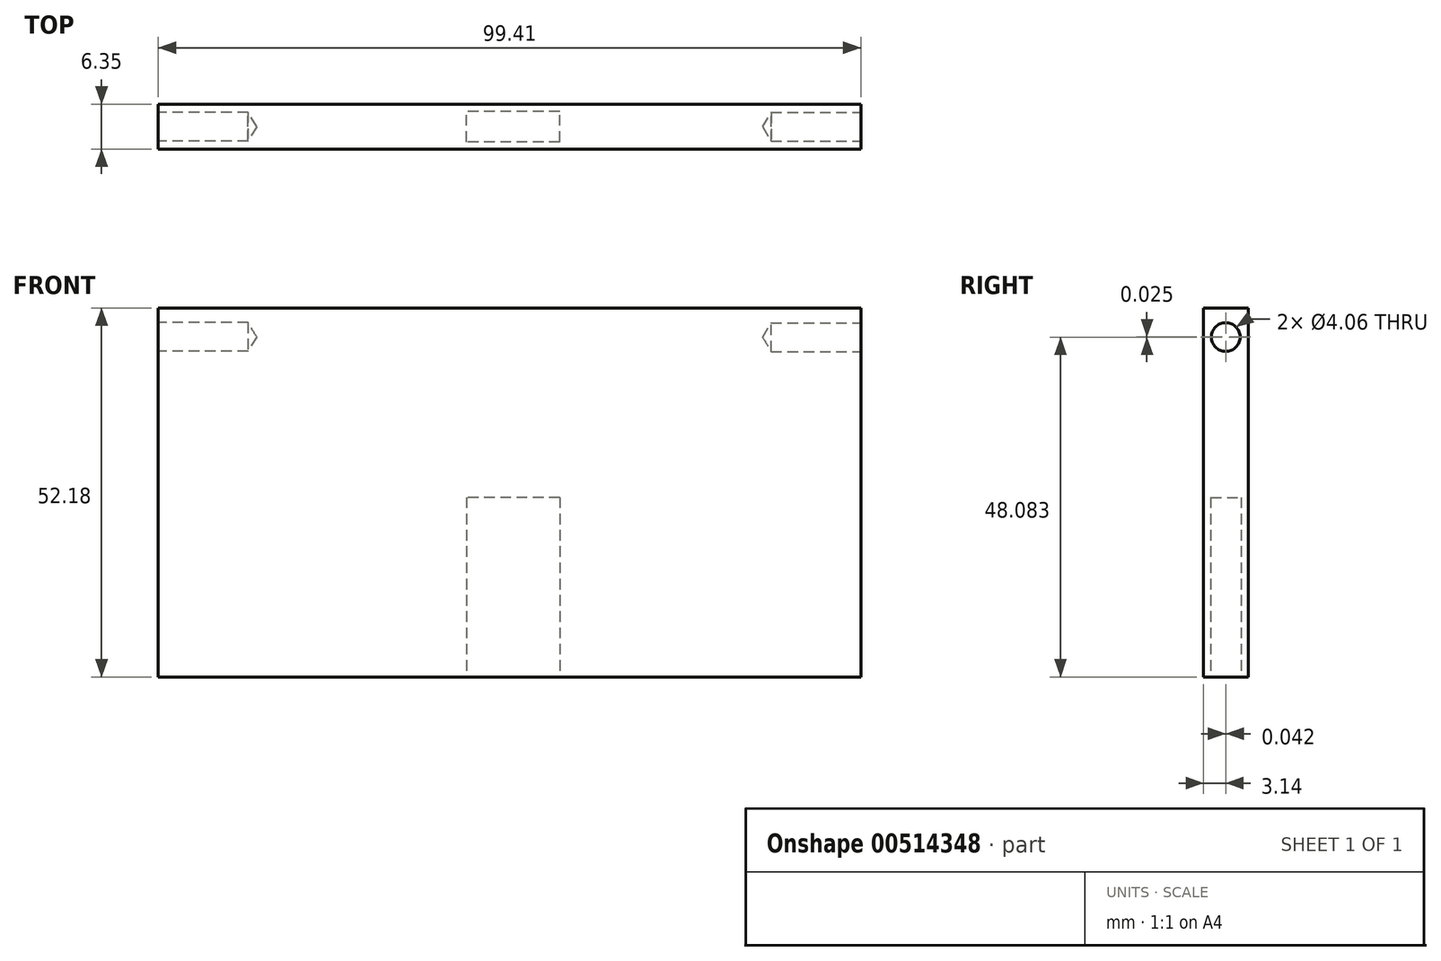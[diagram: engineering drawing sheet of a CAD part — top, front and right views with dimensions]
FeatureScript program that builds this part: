
annotation { "Feature Type Name" : "Feature", "Feature Type Description" : "" }
export const myFeature = defineFeature(function(context is Context, id is Id, definition is map)
    precondition{}
    {
        {
            var Q0;
            Q0=qCreatedBy(makeId("Front.planeOp"),FACE);
            var sketch = newSketch(context, id + "F0", { "sketchPlane" : qUnion([Q0])});
            skLineSegment(sketch, "E0.bottom", {"start": v(-50.2, 52.55) * mm, "end": v(49.21, 52.55) * mm});
            skLineSegment(sketch, "E0.top", {"start": v(-50.2, 0.37) * mm, "end": v(49.21, 0.37) * mm});
            skLineSegment(sketch, "E0.left", {"start": v(-50.2, 52.55) * mm, "end": v(-50.2, 0.37) * mm});
            skLineSegment(sketch, "E0.right", {"start": v(49.21, 52.55) * mm, "end": v(49.21, 0.37) * mm});
            skSolve(sketch);
        }
        {
            var Q0;
            Q0=makeQuery(id+"F0.imprint","IMPRINT",FACE,{"disambiguationData":[TD([[makeQuery(id+"F0.imprint","IMPRINT",EDGE,{"derivedFrom":sQuery(id+"F0.wireOp",EDGE,"E0.bottom")}),-1.0]])]});
            extrude(context, id + "F1", {"entities" : qUnion([Q0]), "depth" : 6.35 * mm});
        }
        {
            var Q0;
            Q0=makeQuery(id+"F1.opExtrude","SWEPT_FACE",FACE,{"disambiguationData":[OSD([sQuery(id+"F0.wireOp",EDGE,"E0.left")])]});
            var sketch = newSketch(context, id + "F2", { "sketchPlane" : qUnion([Q0])});
            skCircle(sketch, "E1", {"center": v(3.17, 48.48) * mm, "radius": 1.98 * mm});
            skSolve(sketch);
        }
        {
            var Q0;
            Q0=makeQuery(id+"F1.opExtrude","SWEPT_FACE",FACE,{"disambiguationData":[OSD([sQuery(id+"F0.wireOp",EDGE,"E0.right")])]});
            var sketch = newSketch(context, id + "F3", { "sketchPlane" : qUnion([Q0])});
            skCircle(sketch, "E2", {"center": v(-3.21, 48.45) * mm, "radius": 1.98 * mm});
            skSolve(sketch);
        }
        {
            var Q0;
            Q0=sQuery(id+"F3.wireOp",VERTEX,"E2.center");
            var Q1;
            Q1=makeQuery(id+"F1.opExtrude","SWEPT_BODY",BODY,{"disambiguationData":[OSD([sQuery(id+"F0.wireOp",EDGE,"E0.bottom"),sQuery(id+"F0.wireOp",EDGE,"E0.top"),sQuery(id+"F0.wireOp",EDGE,"E0.left"),sQuery(id+"F0.wireOp",EDGE,"E0.right")])]});
            hole(context, id + "F4", {"style" : HoleStyle.SIMPLE, "endStyle" : HoleEndStyle.BLIND, "holeDiameter" : 4.06 * mm, "holeDepth" : 12.7 * mm, "isTappedThrough" : true, "tappedDepth" : 12.7 * mm, "tapClearance" : 3, "locations" : qUnion([Q0]), "scope" : qUnion([Q1])});
        }
        {
            var Q0;
            Q0=sQuery(id+"F2.wireOp",VERTEX,"E1.center");
            var Q1;
            Q1=makeQuery(id+"F1.opExtrude","SWEPT_BODY",BODY,{"disambiguationData":[OSD([sQuery(id+"F0.wireOp",EDGE,"E0.bottom"),sQuery(id+"F0.wireOp",EDGE,"E0.top"),sQuery(id+"F0.wireOp",EDGE,"E0.left"),sQuery(id+"F0.wireOp",EDGE,"E0.right")])]});
            hole(context, id + "F5", {"style" : HoleStyle.SIMPLE, "endStyle" : HoleEndStyle.BLIND, "holeDiameter" : 4.06 * mm, "holeDepth" : 12.7 * mm, "isTappedThrough" : true, "tappedDepth" : 12.7 * mm, "tapClearance" : 3, "locations" : qUnion([Q0]), "scope" : qUnion([Q1])});
        }
        {
            var Q0;
            Q0=makeQuery(id+"F1.opExtrude","SWEPT_FACE",FACE,{"disambiguationData":[OSD([sQuery(id+"F0.wireOp",EDGE,"E0.top")])]});
            var sketch = newSketch(context, id + "F6", { "sketchPlane" : qUnion([Q0])});
            skLineSegment(sketch, "E3.bottom", {"start": v(6.6, 5.32) * mm, "end": v(-6.6, 5.32) * mm});
            skLineSegment(sketch, "E3.top", {"start": v(6.6, 1.03) * mm, "end": v(-6.6, 1.03) * mm});
            skLineSegment(sketch, "E3.left", {"start": v(6.6, 5.32) * mm, "end": v(6.6, 1.03) * mm});
            skLineSegment(sketch, "E3.right", {"start": v(-6.6, 5.32) * mm, "end": v(-6.6, 1.03) * mm});
            skLineSegment(sketch, "E4", {"start": v(49.21, 3.18) * mm, "end": v(-50.2, 3.18) * mm, "construction": true});
            skPoint(sketch, "E5", {"position": v(6.6, 3.17) * mm});
            skPoint(sketch, "E6", {"position": v(0, 1.03) * mm});
            skLineSegment(sketch, "E7", {"start": v(0, 0) * mm, "end": v(0, 40.78) * mm, "construction": true});
            skSolve(sketch);
        }
        {
            var Q0;
            Q0=makeQuery(id+"F6.imprint","IMPRINT",FACE,{"disambiguationData":[TD([[makeQuery(id+"F6.imprint","IMPRINT",EDGE,{"derivedFrom":sQuery(id+"F6.wireOp",EDGE,"E3.bottom")}),1.0]])]});
            extrude(context, id + "F7", {"entities" : qUnion([Q0]), "operationType" : NewBodyOperationType.REMOVE, "oppositeDirection" : true, "depth" : 25.4 * mm});
        }
    });
